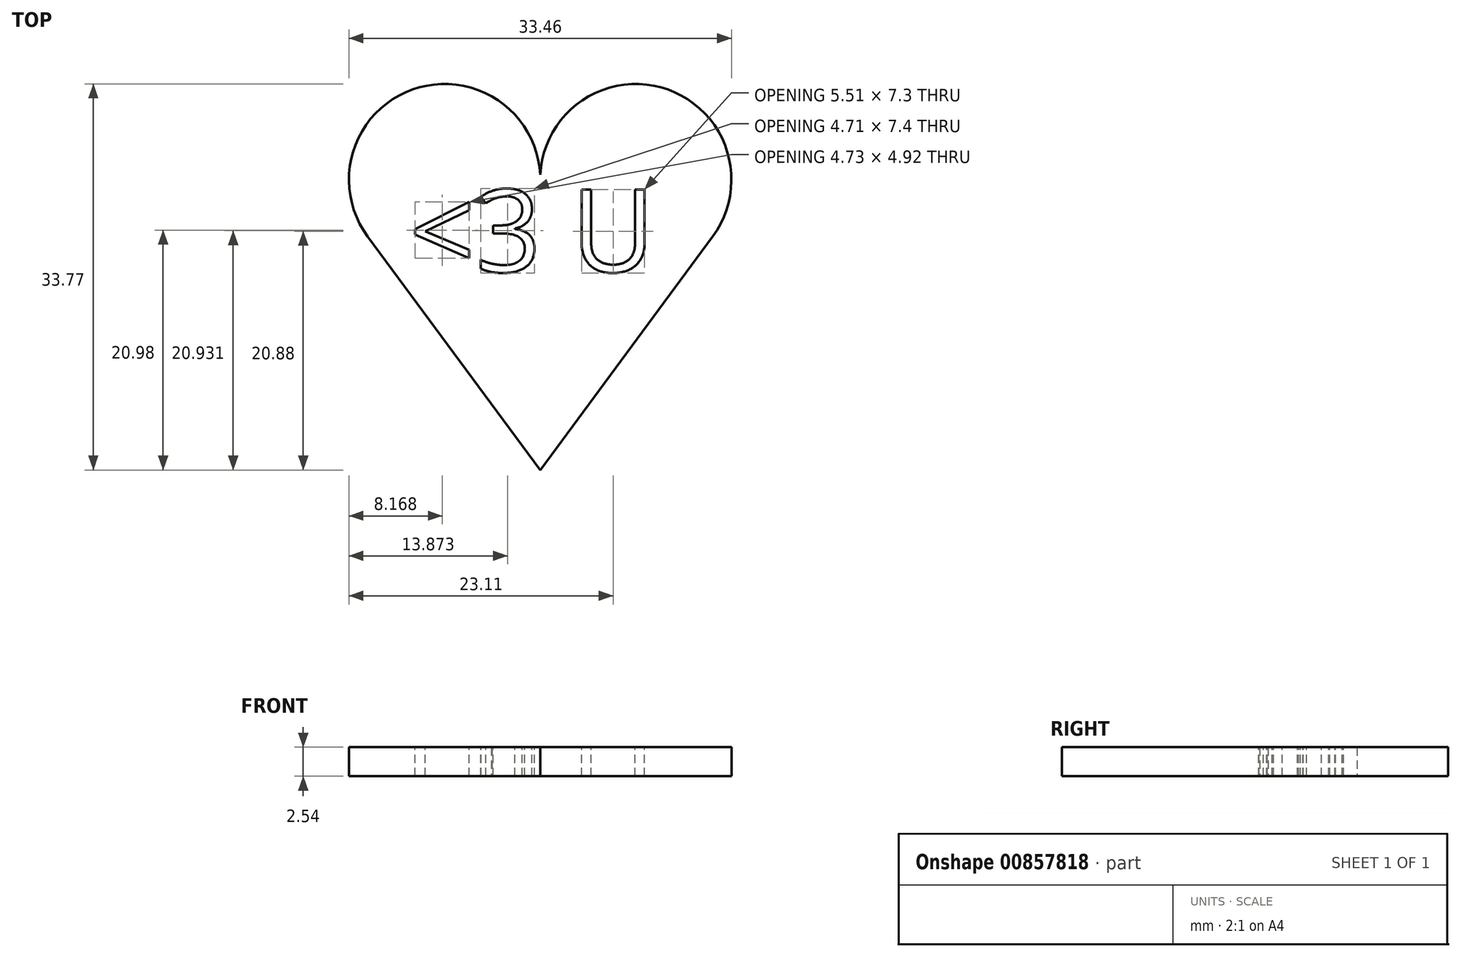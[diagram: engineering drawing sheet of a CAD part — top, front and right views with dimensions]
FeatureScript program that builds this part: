
annotation { "Feature Type Name" : "Feature", "Feature Type Description" : "" }
export const myFeature = defineFeature(function(context is Context, id is Id, definition is map)
    precondition{}
    {
        {
            var Q0;
            Q0=qCreatedBy(makeId("Top.planeOp"),FACE);
            var sketch = newSketch(context, id + "F0", { "sketchPlane" : qUnion([Q0])});
            skCircle(sketch, "E0", {"center": v(8.36, 25.4) * mm, "radius": 8.37 * mm});
            skLineSegment(sketch, "E1", {"start": v(15.1, 20.43) * mm, "end": v(0, 0) * mm});
            skCircle(sketch, "E2.MirrorC", {"center": v(-8.36, 25.4) * mm, "radius": 8.37 * mm});
            skLineSegment(sketch, "E3.MirrorCS", {"start": v(-15.1, 20.43) * mm, "end": v(0, 0) * mm});
            skSolve(sketch);
        }
        {
            var Q0;
            Q0 = qSketchRegion(id + "F0", true);
            extrude(context, id + "F1", {"entities" : qUnion([Q0]), "depth" : 2.54 * mm, "offsetDistance" : 25.4 * mm});
        }
        {
            var Q0;
            Q0=makeQuery(id+"F1.opExtrude","CAP_FACE",FACE,{"disambiguationData":[OSD([sQuery(id+"F0.wireOp",EDGE,"E0"),sQuery(id+"F0.wireOp",EDGE,"E1"),sQuery(id+"F0.wireOp",EDGE,"E2.MirrorC"),sQuery(id+"F0.wireOp",EDGE,"E3.MirrorCS")])],"isStart":false});
            var sketch = newSketch(context, id + "F2", { "sketchPlane" : qUnion([Q0])});
            skText(sketch, "E4", { "text": "<3 U", "fontName": "OpenSans-Regular.ttf"});
            const initialGuessF2  = {"E4": [-0.01144, 0.01733, 1, 0, 0.00726]};
            skSetInitialGuess(sketch, initialGuessF2);
            skSolve(sketch);
        }
        {
            var Q0;
            Q0 = qSketchRegion(id + "F2", true);
            extrude(context, id + "F3", {"entities" : qUnion([Q0]), "operationType" : NewBodyOperationType.REMOVE, "oppositeDirection" : true, "depth" : 25.4 * mm, "offsetDistance" : 25.4 * mm});
        }
    });
